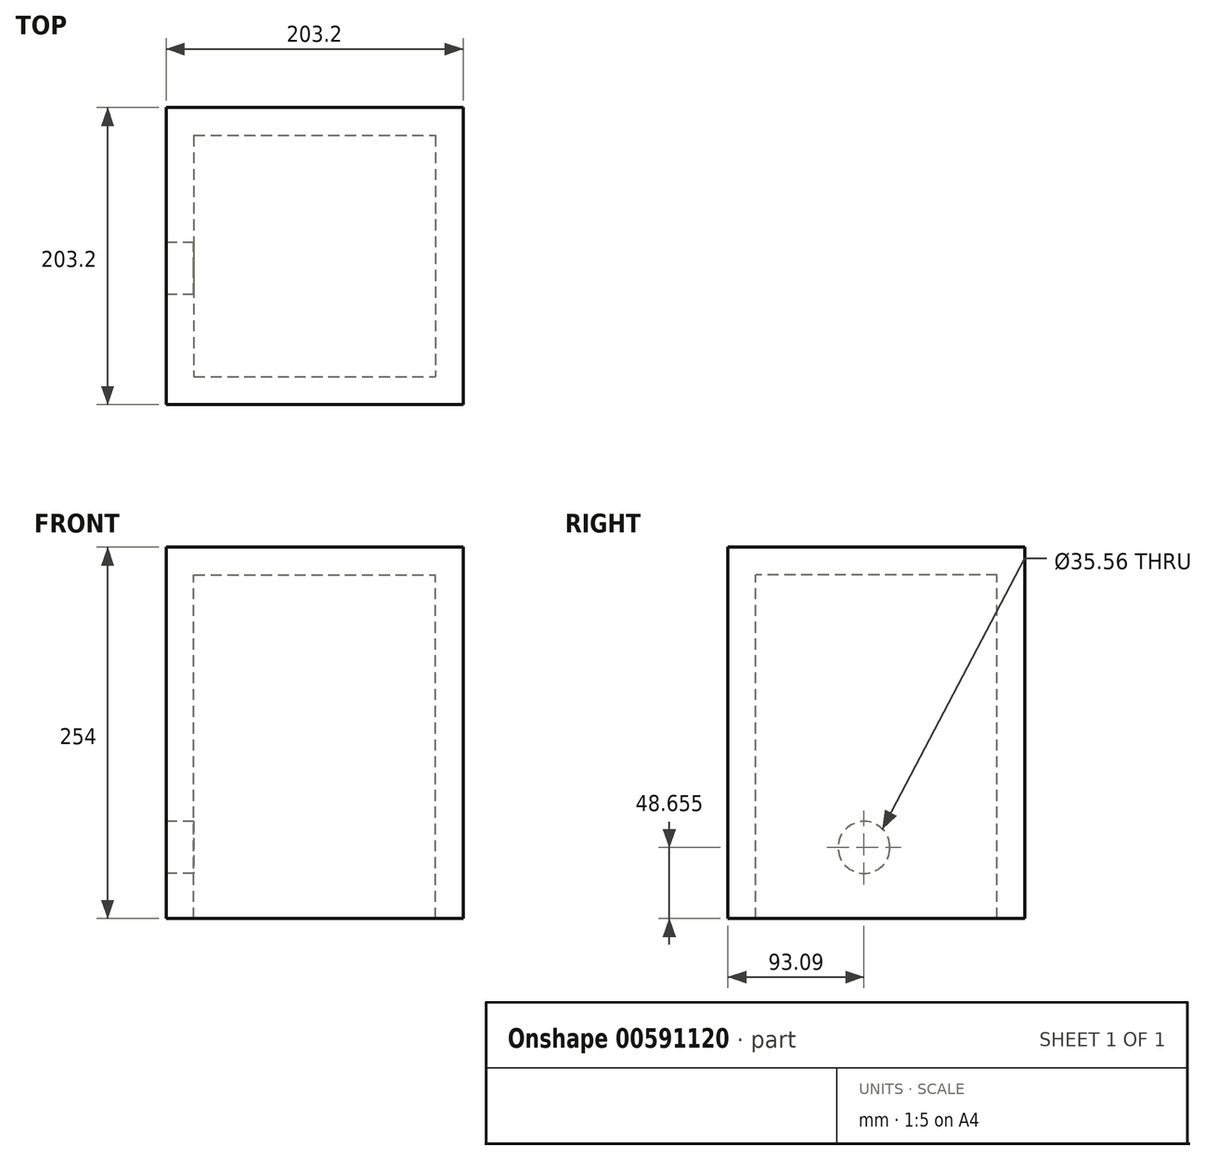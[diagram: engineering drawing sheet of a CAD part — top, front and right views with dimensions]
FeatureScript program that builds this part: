
annotation { "Feature Type Name" : "Feature", "Feature Type Description" : "" }
export const myFeature = defineFeature(function(context is Context, id is Id, definition is map)
    precondition{}
    {
        {
            var Q0;
            Q0=qCreatedBy(makeId("Top.planeOp"),FACE);
            var sketch = newSketch(context, id + "F0", { "sketchPlane" : qUnion([Q0])});
            skLineSegment(sketch, "E0.bottom", {"start": v(-115.8, 110.11) * mm, "end": v(87.4, 110.11) * mm});
            skLineSegment(sketch, "E0.top", {"start": v(-115.8, -93.09) * mm, "end": v(87.4, -93.09) * mm});
            skLineSegment(sketch, "E0.left", {"start": v(-115.8, 110.11) * mm, "end": v(-115.8, -93.09) * mm});
            skLineSegment(sketch, "E0.right", {"start": v(87.4, 110.11) * mm, "end": v(87.4, -93.09) * mm});
            skLineSegment(sketch, "E1.bottom", {"start": v(-96.74, 91.06) * mm, "end": v(68.36, 91.06) * mm});
            skLineSegment(sketch, "E1.top", {"start": v(-96.74, -74.04) * mm, "end": v(68.36, -74.04) * mm});
            skLineSegment(sketch, "E1.left", {"start": v(-96.74, 91.06) * mm, "end": v(-96.74, -74.04) * mm});
            skLineSegment(sketch, "E1.right", {"start": v(68.36, 91.06) * mm, "end": v(68.36, -74.04) * mm});
            skLineSegment(sketch, "E2", {"start": v(0, -74.04) * mm, "end": v(0, -93.09) * mm, "construction": true});
            skLineSegment(sketch, "E3", {"start": v(-115.8, 8.51) * mm, "end": v(-96.74, 8.51) * mm, "construction": true});
            skLineSegment(sketch, "E4", {"start": v(-14.2, 110.11) * mm, "end": v(-14.2, 91.06) * mm, "construction": true});
            skLineSegment(sketch, "E5", {"start": v(68.36, 8.51) * mm, "end": v(87.4, 8.51) * mm, "construction": true});
            skSolve(sketch);
        }
        {
            var Q0;
            Q0=makeQuery(id+"F0.imprint","IMPRINT",FACE,{"disambiguationData":[TD([[makeQuery(id+"F0.imprint","IMPRINT",EDGE,{"derivedFrom":sQuery(id+"F0.wireOp",EDGE,"E0.bottom")}),-1.0]])]});
            extrude(context, id + "F1", {"entities" : qUnion([Q0]), "oppositeDirection" : true, "depth" : 254 * mm, "offsetDistance" : 25.4 * mm});
        }
        {
            var Q0;
            Q0=makeQuery(id+"F0.imprint","IMPRINT",FACE,{"disambiguationData":[TD([[makeQuery(id+"F0.imprint","IMPRINT",EDGE,{"derivedFrom":sQuery(id+"F0.wireOp",EDGE,"E1.bottom")}),-1.0]])]});
            extrude(context, id + "F2", {"entities" : qUnion([Q0]), "operationType" : NewBodyOperationType.ADD, "oppositeDirection" : true, "depth" : 19.05 * mm, "offsetDistance" : 25.4 * mm});
        }
        {
            var Q0;
            Q0=makeQuery(id+"F1.opExtrude","SWEPT_FACE",FACE,{"disambiguationData":[OSD([sQuery(id+"F0.wireOp",EDGE,"E0.left")])]});
            var sketch = newSketch(context, id + "F3", { "sketchPlane" : qUnion([Q0])});
            skCircle(sketch, "E6", {"center": v(0, -205.35) * mm, "radius": 17.78 * mm});
            skSolve(sketch);
        }
        {
            var Q0;
            Q0=makeQuery(id+"F3.imprint","IMPRINT",FACE,{"disambiguationData":[TD([[makeQuery(id+"F3.imprint","IMPRINT",EDGE,{"derivedFrom":sQuery(id+"F3.wireOp",EDGE,"E6")}),1.0]])]});
            extrude(context, id + "F4", {"entities" : qUnion([Q0]), "operationType" : NewBodyOperationType.REMOVE, "oppositeDirection" : true, "depth" : 25.4 * mm, "offsetDistance" : 25.4 * mm});
        }
    });
